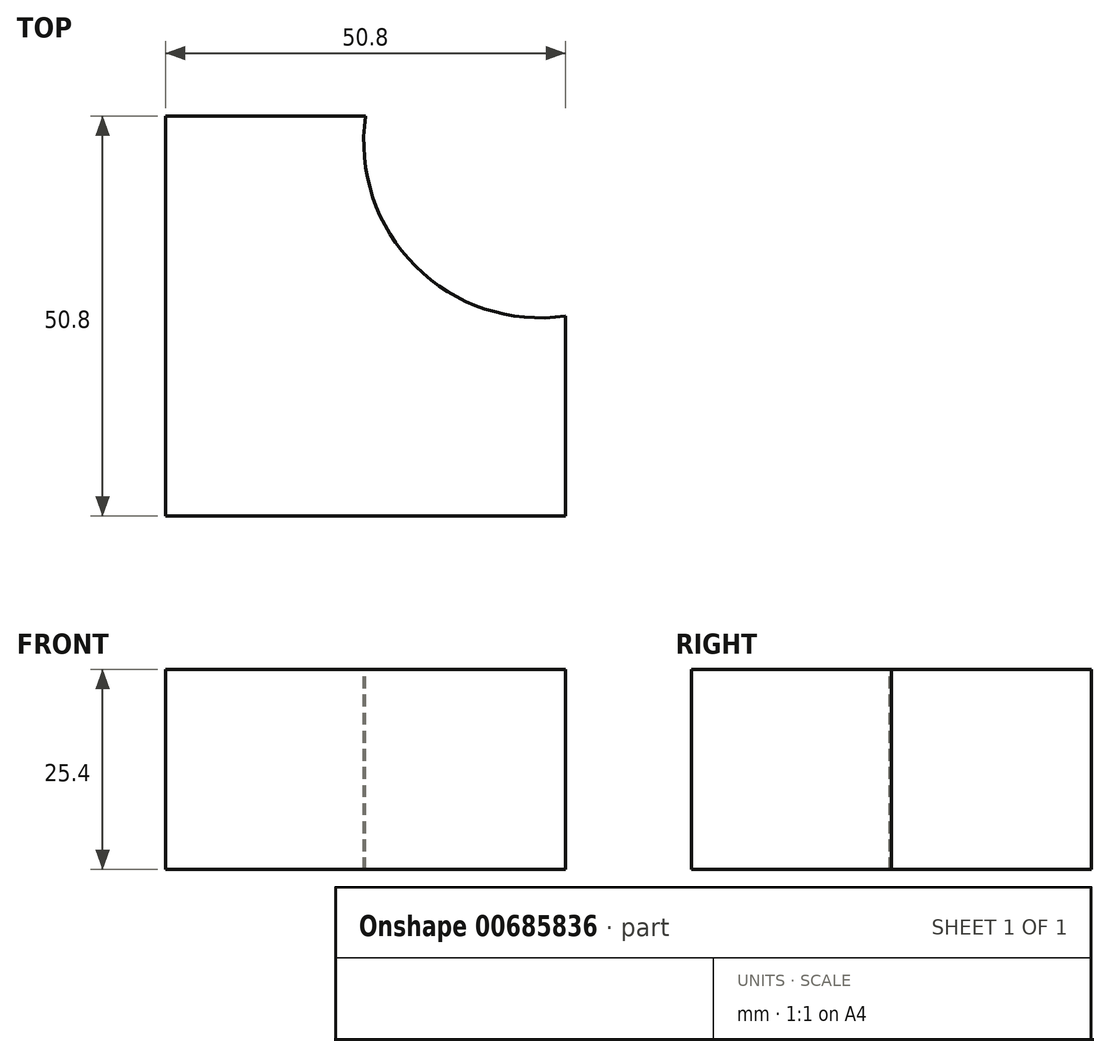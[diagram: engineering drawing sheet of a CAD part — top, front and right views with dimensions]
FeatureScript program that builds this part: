
annotation { "Feature Type Name" : "Feature", "Feature Type Description" : "" }
export const myFeature = defineFeature(function(context is Context, id is Id, definition is map)
    precondition{}
    {
        {
            var Q0;
            Q0=qCreatedBy(makeId("Top.planeOp"),FACE);
            var sketch = newSketch(context, id + "F0", { "sketchPlane" : qUnion([Q0])});
            skLineSegment(sketch, "E0.bottom", {"start": v(32.3, -16.86) * mm, "end": v(-18.5, -16.86) * mm});
            skLineSegment(sketch, "E0.top", {"start": v(32.3, 33.94) * mm, "end": v(-18.5, 33.94) * mm});
            skLineSegment(sketch, "E0.left", {"start": v(32.3, -16.86) * mm, "end": v(32.3, 33.94) * mm});
            skLineSegment(sketch, "E0.right", {"start": v(-18.5, -16.86) * mm, "end": v(-18.5, 33.94) * mm});
            skSolve(sketch);
        }
        {
            var Q0;
            Q0 = qSketchRegion(id + "F0", true);
            extrude(context, id + "F1", {"entities" : qUnion([Q0]), "depth" : 25.4 * mm, "offsetDistance" : 25.4 * mm});
        }
        {
            var Q0;
            Q0=makeQuery(id+"F1.opExtrude","CAP_FACE",FACE,{"disambiguationData":[OSD([sQuery(id+"F0.wireOp",EDGE,"E0.bottom"),sQuery(id+"F0.wireOp",EDGE,"E0.top"),sQuery(id+"F0.wireOp",EDGE,"E0.left"),sQuery(id+"F0.wireOp",EDGE,"E0.right")])],"isStart":false});
            var sketch = newSketch(context, id + "F2", { "sketchPlane" : qUnion([Q0])});
            skLineSegment(sketch, "E1", {"start": v(32.3, -16.86) * mm, "end": v(32.3, 8.54) * mm});
            skLineSegment(sketch, "E2", {"start": v(-18.5, 33.94) * mm, "end": v(6.9, 33.94) * mm});
            skArc(sketch, "E3", {"start": v(6.9, 33.94) * mm, "mid": v(13.25, 14.87) * mm, "end": v(32.3, 8.54) * mm});
            skSolve(sketch);
        }
        {
            var Q0;
            Q0 = qSketchRegion(id + "F2", true);
            var Q1;
            {var subQ0=sQuery(id+"F2.wireOp",EDGE,"E3");Q1=makeQuery(id+"F2.imprint","IMPRINT",FACE,{"disambiguationData":[TD([[makeQuery(id+"F2.imprint","IMPRINT",EDGE,{"derivedFrom":subQ0}),1.0]])]});}
            extrude(context, id + "F3", {"entities" : qUnion([Q0, Q1]), "operationType" : NewBodyOperationType.REMOVE, "oppositeDirection" : true, "depth" : 25.4 * mm, "offsetDistance" : 25.4 * mm});
        }
    });
